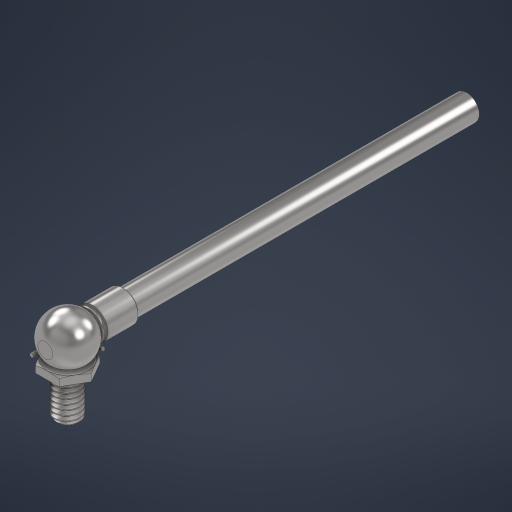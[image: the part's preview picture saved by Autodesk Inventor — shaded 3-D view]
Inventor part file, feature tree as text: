
AUTODESK INVENTOR PART (.ipt)
format: ipt  version: 2024 (Build 280153000, 153)  size: 770,560 bytes
history: native  units: in
note: dims shown in document units (in); Inventor stores cm internally (conversion verified against a paired STEP export)
features: other x3, revolve x1, sweep x1
ambient origin geometry x8: Origin, YZ Plane, XZ Plane, XY Plane, X Axis, Y Axis, Z Axis, Center Point
bodies: Solid2 (feature_tree), Solid4 (feature_tree), Solid5 (feature_tree), Solid8 (feature_tree), Solid9 (feature_tree)
feature tree (5):
  other  "Cut-Extrude2"
  other  "Boss-Extrude2[1]"
  revolve  "Revolve2[1]"  [1 undecoded]
  sweep  "Sweep3"
  other  "Split1[3]"
note: 1 required parameter value undecoded (feature->parameter linkage not recoverable at this tier; creation-order binding heuristic only, values carry confidence <= 0.55)
